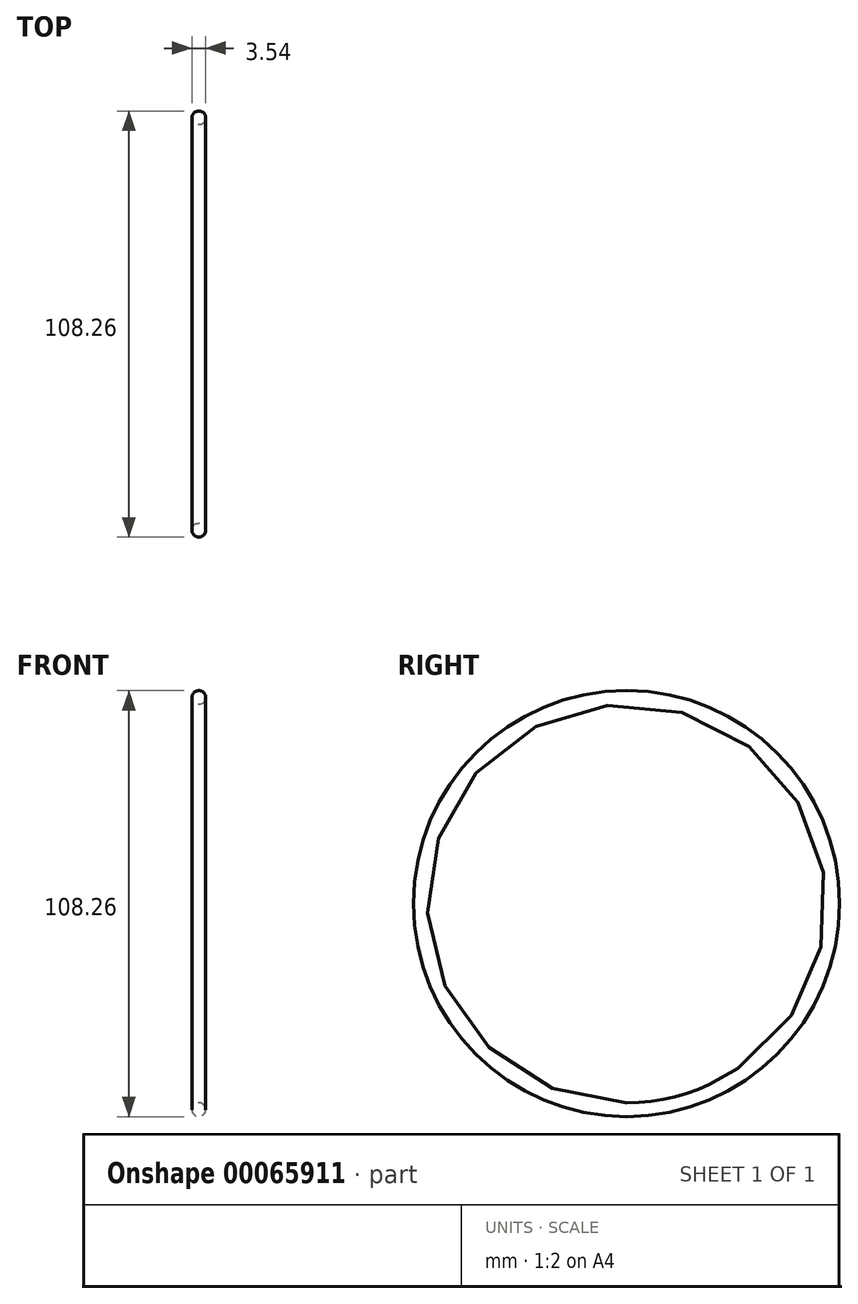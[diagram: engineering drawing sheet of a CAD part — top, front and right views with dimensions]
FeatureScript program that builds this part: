
annotation { "Feature Type Name" : "Feature", "Feature Type Description" : "" }
export const myFeature = defineFeature(function(context is Context, id is Id, definition is map)
    precondition{}
    {
        {
            var Q0;
            Q0=qCreatedBy(makeId("Front.planeOp"),FACE);
            var sketch = newSketch(context, id + "F0", { "sketchPlane" : qUnion([Q0])});
            skLineSegment(sketch, "E0", {"start": v(0, 0) * mm, "end": v(-6.06, 0) * mm, "construction": true});
            skCircle(sketch, "E1", {"center": v(0, 52.36) * mm, "radius": 1.77 * mm});
            skSolve(sketch);
        }
        {
            var Q0;
            Q0=makeQuery(id+"F0.imprint","IMPRINT",FACE,{"disambiguationData":[TD([[makeQuery(id+"F0.imprint","IMPRINT",EDGE,{"derivedFrom":sQuery(id+"F0.wireOp",EDGE,"E1")}),1.0]])]});
            var Q1;
            Q1=sQuery(id+"F0.wireOp",EDGE,"E0");
            revolve(context, id + "F1", {"entities" : qUnion([Q0]), "axis" : qUnion([Q1]), "revolveType" : RevolveType.FULL});
        }
    });
